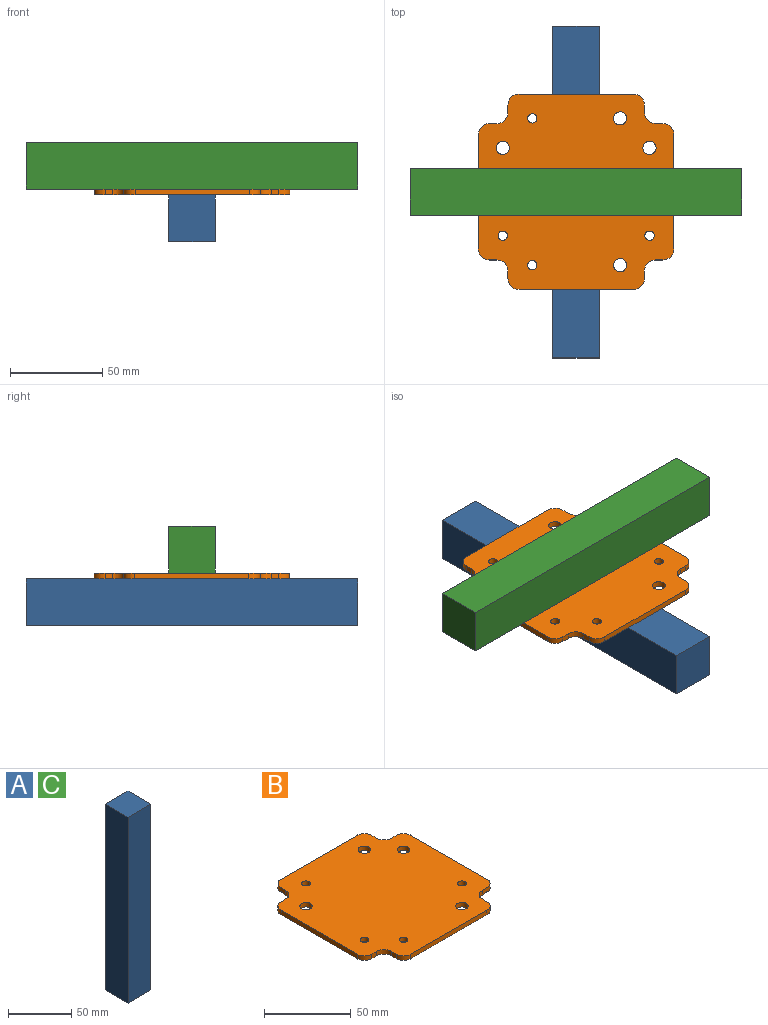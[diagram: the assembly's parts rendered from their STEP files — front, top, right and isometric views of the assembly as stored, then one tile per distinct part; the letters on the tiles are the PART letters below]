
ASSEMBLY  parts=3 mates=2
PART A: 6 faces, bbox 25.4x25.4x180 mm
  f0: plane 180x25.4mm, normal (0,1,0), area 4572mm2, adj f1,f3,f4,f5
  f1: plane 180x25.4mm, normal (-1,0,0), area 4572mm2, adj f0,f2,f4,f5
  f2: plane 180x25.4mm, normal (0,-1,0), area 4572mm2, adj f1,f3,f4,f5
  f3: plane 180x25.4mm, normal (1,0,0), area 4572mm2, adj f0,f2,f4,f5
  f4: plane 25.4x25.4mm, normal (0,0,1), area 645.2mm2, adj f0,f1,f2,f3
  f5: plane 25.4x25.4mm, normal (0,0,-1), area 645.2mm2, adj f0,f1,f2,f3
PART B: 34 faces, bbox 106x106x3.2 mm
  f0: plane 4x3.18mm, normal (0,1,0), area 12.7mm2, adj f20,f21,f22,f33
  f1: plane 4x3.18mm, normal (1,0,0), area 12.7mm2, adj f20,f21,f22,f23
  f2: plane 62x3.18mm, normal (0,1,0), area 196.8mm2, adj f20,f21,f23,f24
  f3: plane 4x3.18mm, normal (-1,0,0), area 12.7mm2, adj f20,f21,f24,f25
  f4: plane 4x3.18mm, normal (0,1,0), area 12.7mm2, adj f20,f21,f25,f26
  f5: plane 62x3.18mm, normal (-1,0,0), area 196.8mm2, adj f20,f21,f26,f27
  f6: plane 4x3.18mm, normal (0,-1,0), area 12.7mm2, adj f20,f21,f27,f28
  f7: plane 4x3.18mm, normal (-1,0,0), area 12.7mm2, adj f20,f21,f28,f29
  f8: plane 62x3.18mm, normal (0,-1,0), area 196.8mm2, adj f20,f21,f29,f30
  f9: plane 4x3.18mm, normal (1,0,0), area 12.7mm2, adj f20,f21,f30,f31
  f10: plane 4x3.18mm, normal (0,-1,0), area 12.7mm2, adj f20,f21,f31,f32
  f11: cylinder r=3.59mm len=7.18mm, axis (0,0,-1), area 71.6mm2, adj f20,f21
  f12: cylinder r=2.52mm len=5.05mm, axis (0,0,-1), area 50.4mm2, adj f20,f21
  f13: cylinder r=3.59mm len=7.18mm, axis (0,0,-1), area 71.6mm2, adj f20,f21
  f14: cylinder r=3.59mm len=7.18mm, axis (0,0,-1), area 71.6mm2, adj f20,f21
  f15: cylinder r=2.52mm len=5.05mm, axis (0,0,-1), area 50.4mm2, adj f20,f21
  f16: cylinder r=3.59mm len=7.18mm, axis (0,0,-1), area 71.6mm2, adj f20,f21
  f17: cylinder r=2.52mm len=5.05mm, axis (0,0,-1), area 50.4mm2, adj f20,f21
  f18: plane 62x3.18mm, normal (1,0,0), area 196.8mm2, adj f20,f21,f32,f33
  f19: cylinder r=2.52mm len=5.05mm, axis (0,0,-1), area 50.4mm2, adj f20,f21
  f20: plane 106x106mm, normal (0,0,1), area 9939mm2, adj f0,f1,f2,f3,f4,f5,f6,f7
  f21: plane 106x106mm, normal (0,0,-1), area 9939mm2, adj f0,f1,f2,f3,f4,f5,f6,f7
  f22: cylinder r=6mm len=6mm, axis (0,0,1), area 29.9mm2, adj f0,f1,f20,f21
  f23: cylinder r=6mm len=6mm, axis (0,0,-1), area 29.9mm2, adj f1,f2,f20,f21
  f24: cylinder r=6mm len=6mm, axis (0,0,1), area 29.9mm2, adj f2,f3,f20,f21
  f25: cylinder r=6mm len=6mm, axis (0,0,-1), area 29.9mm2, adj f3,f4,f20,f21
  f26: cylinder r=6mm len=6mm, axis (0,0,1), area 29.9mm2, adj f4,f5,f20,f21
  f27: cylinder r=6mm len=6mm, axis (0,0,-1), area 29.9mm2, adj f5,f6,f20,f21
  f28: cylinder r=6mm len=6mm, axis (0,0,1), area 29.9mm2, adj f6,f7,f20,f21
  f29: cylinder r=6mm len=6mm, axis (0,0,-1), area 29.9mm2, adj f7,f8,f20,f21
  f30: cylinder r=6mm len=6mm, axis (0,0,1), area 29.9mm2, adj f8,f9,f20,f21
  f31: cylinder r=6mm len=6mm, axis (0,0,-1), area 29.9mm2, adj f9,f10,f20,f21
  f32: cylinder r=6mm len=6mm, axis (0,0,1), area 29.9mm2, adj f10,f18,f20,f21
  f33: cylinder r=6mm len=6mm, axis (0,0,-1), area 29.9mm2, adj f0,f18,f20,f21
PART C: same geometry as A
PLACE A rot(axis=(1,0,0),90deg) t=(44.4,98.61,-43.47)mm
PLACE B t=(24.9,8.71,-10.08)mm fixed
PLACE C rot(axis=(0.71,0,-0.71),180deg) t=(114.8,29.31,-13.81)mm
MATE planar C.f3 <-> B.f20  axis (0,0,-1) through (24.8,8.61,-6.91)mm
MATE planar A.f0 <-> B.f21  axis (0,0,1) through (24.8,8.61,-10.08)mm
